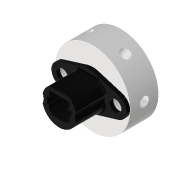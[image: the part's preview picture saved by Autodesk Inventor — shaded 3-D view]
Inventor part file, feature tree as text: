
AUTODESK INVENTOR PART (.ipt)
format: ipt  version: 2022 (Build 260153000, 153)  size: 217,600 bytes
history: native  units: in
note: dims shown in document units (in); Inventor stores cm internally (conversion verified against a paired STEP export)
features: reference x7, other x5, extrude x2, sketch x2, pattern_circular x1
ambient origin geometry x8: Origin, YZ Plane, XZ Plane, XY Plane, X Axis, Y Axis, Z Axis, Center Point
bodies: Volumenkörper1 (feature_tree)
feature tree (17):
  other  "00_toslink_launcher_v3"
  extrude  "Extrusion1"  Depth=0.3543in TaperAngle=0.0deg
  extrude  "Extrusion2"  Depth=0.3543in TaperAngle=0.0deg
  pattern_circular  "Runde Anordnung1"  Count=6 Angle=360.0deg
  sketch  "Skizze1"  dims[d0=0.2756in d1=0.3543in d2=0.0in]
  reference  "Referenz1"
  reference  "Referenz2"
  reference  "Referenz3"
  reference  "Referenz4"
  reference  "Referenz5"
  reference  "Referenz6"
  reference  "Referenz7"
  sketch  "Skizze2"  dims[d3=0.1102in d4=0.3543in d5=0.1772in d6=0.0in d7=0.0in d8=2.3622in d9=360.0deg]
  other  "MeshFeature1"
  other  "Spectroscope_v0.iam"
  other  "Spectrometer_pinholeholder_v0:1"
  other  "00_mk8_nozzle_0.4STEP:1"
